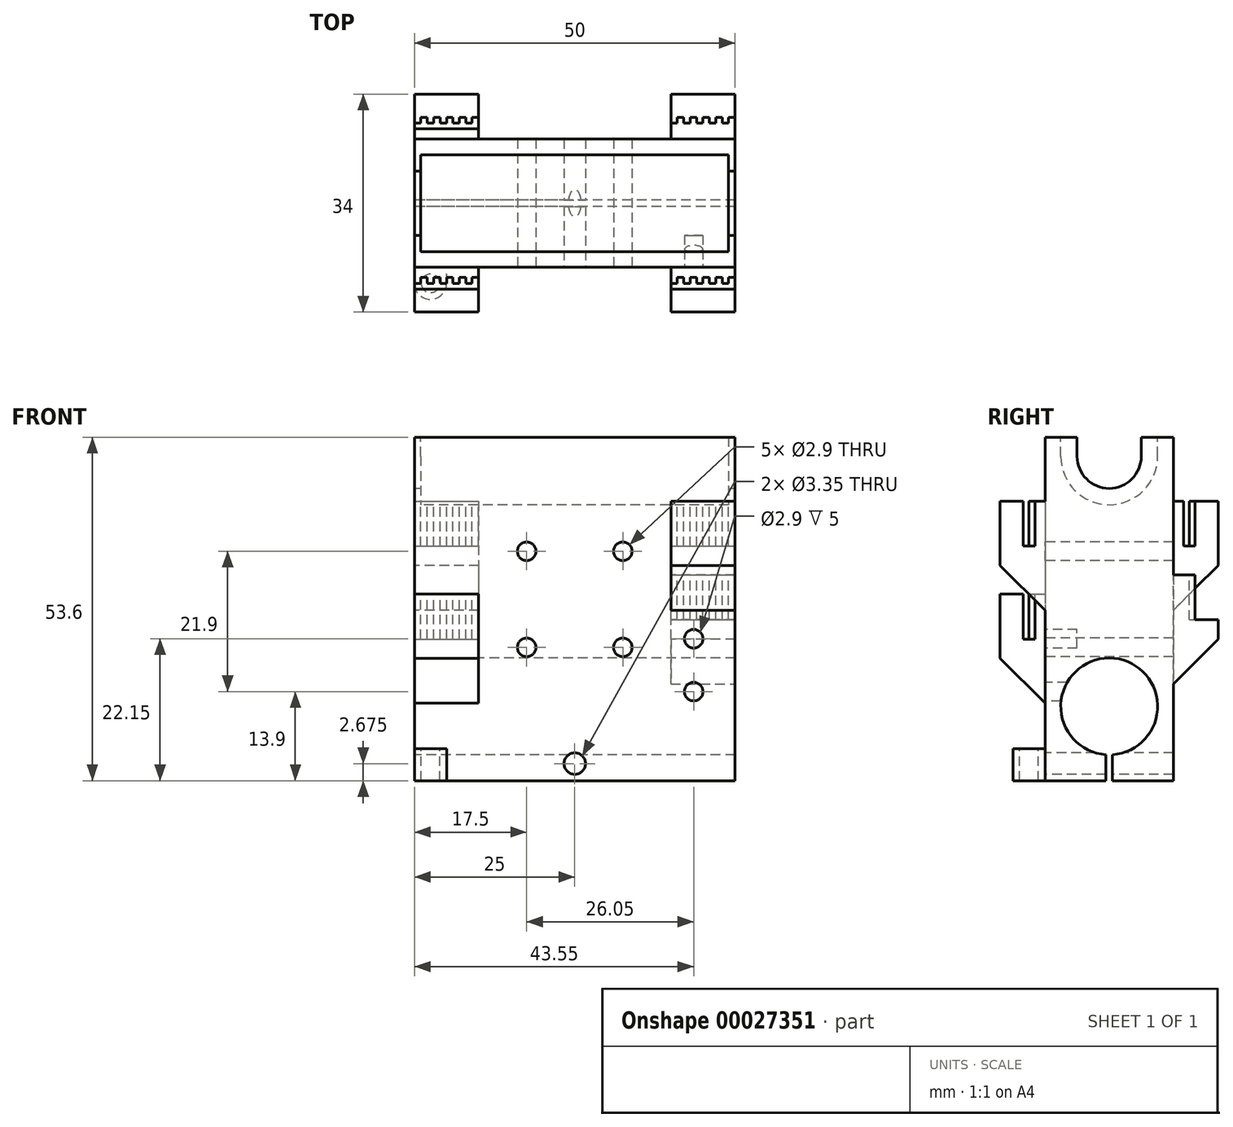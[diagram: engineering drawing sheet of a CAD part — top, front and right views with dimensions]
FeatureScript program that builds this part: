
annotation { "Feature Type Name" : "Feature", "Feature Type Description" : "" }
export const myFeature = defineFeature(function(context is Context, id is Id, definition is map)
    precondition{}
    {
        {
            var Q0;
            Q0=qCreatedBy(makeId("Top.planeOp"),FACE);
            var sketch = newSketch(context, id + "F0", { "sketchPlane" : qUnion([Q0])});
            skLineSegment(sketch, "E0.bottom", {"start": v(0, 0) * mm, "end": v(50, 0) * mm});
            skLineSegment(sketch, "E0.top", {"start": v(0, 20) * mm, "end": v(50, 20) * mm});
            skLineSegment(sketch, "E0.left", {"start": v(0, 0) * mm, "end": v(0, 20) * mm});
            skLineSegment(sketch, "E0.right", {"start": v(50, 0) * mm, "end": v(50, 20) * mm});
            skSolve(sketch);
        }
        {
            var Q0;
            Q0=qSketchRegion(id+"F0",true);
            extrude(context, id + "F1", {"entities" : qUnion([Q0]), "depth" : 50.6 * mm, "hasSecondDirection" : true, "secondDirectionOppositeDirection" : true, "secondDirectionDepth" : 3 * mm});
        }
        {
            var Q0;
            Q0=makeQuery(id+"F1.opExtrude","SWEPT_FACE",FACE,{"disambiguationData":[OSD([sQuery(id+"F0.wireOp",EDGE,"E0.left")])]});
            var sketch = newSketch(context, id + "F2", { "sketchPlane" : qUnion([Q0])});
            skCircle(sketch, "E1", {"center": v(-10, 8.6) * mm, "radius": 7.55 * mm});
            skCircle(sketch, "E2", {"center": v(-10, 47.6) * mm, "radius": 5 * mm});
            skLineSegment(sketch, "E3", {"start": v(-20, 47.6) * mm, "end": v(0, 47.6) * mm, "construction": true});
            skLineSegment(sketch, "E4", {"start": v(-15, 50.6) * mm, "end": v(-15, 47.6) * mm});
            skLineSegment(sketch, "E5", {"start": v(-5, 50.6) * mm, "end": v(-5, 47.6) * mm});
            skLineSegment(sketch, "E6", {"start": v(-20, 8.6) * mm, "end": v(0, 8.6) * mm, "construction": true});
            skLineSegment(sketch, "E7", {"start": v(-10, 8.6) * mm, "end": v(-10, -3) * mm, "construction": true});
            skLineSegment(sketch, "E8", {"start": v(-10, -3) * mm, "end": v(-10.5, -3) * mm});
            skLineSegment(sketch, "E9", {"start": v(-10.5, -3) * mm, "end": v(-10.5, 1.07) * mm});
            skLineSegment(sketch, "E10", {"start": v(-10.5, 1.07) * mm, "end": v(-9.5, 1.07) * mm});
            skLineSegment(sketch, "E11", {"start": v(-9.5, 1.07) * mm, "end": v(-9.5, 0) * mm});
            skLineSegment(sketch, "E12", {"start": v(-9.5, -3) * mm, "end": v(-10, -3) * mm});
            skLineSegment(sketch, "E13", {"start": v(-10, 15.6) * mm, "end": v(-10, 16.15) * mm});
            skLineSegment(sketch, "E14", {"start": v(-10, 15.6) * mm, "end": v(-5.53, 14.68) * mm});
            skLineSegment(sketch, "E15", {"start": v(-10, 15.6) * mm, "end": v(-14.47, 14.68) * mm});
            skCircle(sketch, "E16", {"center": v(-10, 47.6) * mm, "radius": 7.55 * mm});
            skLineSegment(sketch, "E17", {"start": v(-2.45, 47.6) * mm, "end": v(-2.45, 50.6) * mm});
            skLineSegment(sketch, "E18", {"start": v(-17.55, 47.6) * mm, "end": v(-17.55, 50.6) * mm});
            skLineSegment(sketch, "E19", {"start": v(-9.5, -3) * mm, "end": v(-9.5, 0) * mm});
            skSolve(sketch);
        }
        {
            var Q0;
            {var subQ0=sQuery(id+"F2.wireOp",EDGE,"E14");var subQ1=sQuery(id+"F2.wireOp",EDGE,"E1");var subQ3=makeQuery(id+"F2.imprint","INTERSECT",VERTEX,{"disambiguationData":[OD(0.0)],"derivedFrom":[subQ1,subQ0]});Q0=makeQuery(id+"F2.imprint","IMPRINT",FACE,{"disambiguationData":[TD([[makeQuery(id+"F2.imprint","IMPRINT",EDGE,{"disambiguationData":[TD([[subQ3,-1.0]])],"derivedFrom":subQ1}),1.0]])]});}
            var Q1;
            {var subQ0=sQuery(id+"F2.wireOp",EDGE,"E15");var subQ1=sQuery(id+"F2.wireOp",EDGE,"E1");var subQ3=makeQuery(id+"F2.imprint","INTERSECT",VERTEX,{"disambiguationData":[OD(0.0)],"derivedFrom":[subQ1,subQ0]});Q1=makeQuery(id+"F2.imprint","IMPRINT",FACE,{"disambiguationData":[TD([[makeQuery(id+"F2.imprint","IMPRINT",EDGE,{"disambiguationData":[TD([[subQ3,1.0]])],"derivedFrom":subQ1}),1.0]])]});}
            var Q2;
            Q2=makeQuery(id+"F2.imprint","IMPRINT",FACE,{"disambiguationData":[TD([[makeQuery(id+"F2.imprint","IMPRINT",EDGE,{"derivedFrom":sQuery(id+"F2.wireOp",EDGE,"E8")}),-1.0]])]});
            var Q3;
            {var subQ0=sQuery(id+"F2.wireOp",EDGE,"E10");Q3=makeQuery(id+"F2.imprint","IMPRINT",FACE,{"disambiguationData":[TD([[makeQuery(id+"F2.imprint","IMPRINT",EDGE,{"derivedFrom":subQ0}),-1.0]])]});}
            var Q4;
            {var subQ3=sQuery(id+"F2.wireOp",EDGE,"E13");Q4=makeQuery(id+"F2.imprint","IMPRINT",FACE,{"disambiguationData":[TD([[makeQuery(id+"F2.imprint","IMPRINT",EDGE,{"derivedFrom":subQ3}),-1.0]])]});}
            var Q5;
            {var subQ3=sQuery(id+"F2.wireOp",EDGE,"E13");Q5=makeQuery(id+"F2.imprint","IMPRINT",FACE,{"disambiguationData":[TD([[makeQuery(id+"F2.imprint","IMPRINT",EDGE,{"derivedFrom":subQ3}),1.0]])]});}
            var Q6;
            {var subQ7=sQuery(id+"F2.wireOp",EDGE,"E10");Q6=makeQuery(id+"F2.imprint","IMPRINT",FACE,{"disambiguationData":[TD([[makeQuery(id+"F2.imprint","IMPRINT",EDGE,{"derivedFrom":subQ7}),1.0]])]});}
            var Q7;
            {var subQ3=sQuery(id+"F2.wireOp",EDGE,"E5");Q7=makeQuery(id+"F2.imprint","IMPRINT",FACE,{"disambiguationData":[TD([[makeQuery(id+"F2.imprint","IMPRINT",EDGE,{"derivedFrom":subQ3}),-1.0]])]});}
            var Q8;
            {var subQ0=sQuery(id+"F2.wireOp",EDGE,"E4");Q8=makeQuery(id+"F2.imprint","IMPRINT",FACE,{"disambiguationData":[TD([[makeQuery(id+"F2.imprint","IMPRINT",EDGE,{"derivedFrom":subQ0}),1.0]])]});}
            var Q9;
            {var subQ0=sQuery(id+"F2.wireOp",EDGE,"E4");Q9=makeQuery(id+"F2.imprint","IMPRINT",FACE,{"disambiguationData":[TD([[makeQuery(id+"F2.imprint","IMPRINT",EDGE,{"derivedFrom":subQ0}),1.0]])]});}
            var Q10;
            {var subQ3=sQuery(id+"F2.wireOp",EDGE,"E5");Q10=makeQuery(id+"F2.imprint","IMPRINT",FACE,{"disambiguationData":[TD([[makeQuery(id+"F2.imprint","IMPRINT",EDGE,{"derivedFrom":subQ3}),-1.0]])]});}
            var Q11;
            {var subQ1=sQuery(id+"F2.wireOp",EDGE,"E2");var subQ4=makeQuery(id+"F2.imprint","INTERSECT",VERTEX,{"derivedFrom":[subQ1,sQuery(id+"F2.wireOp",EDGE,"E5")]});Q11=makeQuery(id+"F2.imprint","IMPRINT",FACE,{"disambiguationData":[TD([[makeQuery(id+"F2.imprint","IMPRINT",EDGE,{"disambiguationData":[TD([[subQ4,-1.0]])],"derivedFrom":subQ1}),1.0]])]});}
            extrude(context, id + "F3", {"entities" : qUnion([Q0, Q1, Q2, Q3, Q4, Q5, Q6, Q7, Q8, Q9, Q10, Q11]), "operationType" : NewBodyOperationType.REMOVE, "endBound" : BoundingType.THROUGH_ALL, "oppositeDirection" : true, "depth" : 25 * mm});
        }
        {
            var Q0;
            {var subQ3=sQuery(id+"F2.wireOp",EDGE,"E4");Q0=makeQuery(id+"F2.imprint","IMPRINT",FACE,{"disambiguationData":[TD([[makeQuery(id+"F2.imprint","IMPRINT",EDGE,{"derivedFrom":subQ3}),-1.0]])]});}
            var Q1;
            {var subQ3=sQuery(id+"F2.wireOp",EDGE,"E18");Q1=makeQuery(id+"F2.imprint","IMPRINT",FACE,{"disambiguationData":[TD([[makeQuery(id+"F2.imprint","IMPRINT",EDGE,{"derivedFrom":subQ3}),-1.0]])]});}
            var Q2;
            {var subQ3=sQuery(id+"F2.wireOp",EDGE,"E17");Q2=makeQuery(id+"F2.imprint","IMPRINT",FACE,{"disambiguationData":[TD([[makeQuery(id+"F2.imprint","IMPRINT",EDGE,{"derivedFrom":subQ3}),1.0]])]});}
            extrude(context, id + "F4", {"entities" : qUnion([Q0, Q1, Q2]), "operationType" : NewBodyOperationType.REMOVE, "oppositeDirection" : true, "depth" : 49 * mm});
        }
        {
            var Q0;
            {var subQ3=sQuery(id+"F2.wireOp",EDGE,"E4");Q0=makeQuery(id+"F2.imprint","IMPRINT",FACE,{"disambiguationData":[TD([[makeQuery(id+"F2.imprint","IMPRINT",EDGE,{"derivedFrom":subQ3}),-1.0]])]});}
            var Q1;
            {var subQ3=sQuery(id+"F2.wireOp",EDGE,"E18");Q1=makeQuery(id+"F2.imprint","IMPRINT",FACE,{"disambiguationData":[TD([[makeQuery(id+"F2.imprint","IMPRINT",EDGE,{"derivedFrom":subQ3}),-1.0]])]});}
            var Q2;
            {var subQ3=sQuery(id+"F2.wireOp",EDGE,"E17");Q2=makeQuery(id+"F2.imprint","IMPRINT",FACE,{"disambiguationData":[TD([[makeQuery(id+"F2.imprint","IMPRINT",EDGE,{"derivedFrom":subQ3}),1.0]])]});}
            extrude(context, id + "F5", {"entities" : qUnion([Q0, Q1, Q2]), "operationType" : NewBodyOperationType.ADD, "oppositeDirection" : true, "depth" : 16.21 * mm});
        }
        {
            var Q0;
            {var subQ3=sQuery(id+"F2.wireOp",EDGE,"E4");Q0=makeQuery(id+"F2.imprint","IMPRINT",FACE,{"disambiguationData":[TD([[makeQuery(id+"F2.imprint","IMPRINT",EDGE,{"derivedFrom":subQ3}),-1.0]])]});}
            var Q1;
            {var subQ3=sQuery(id+"F2.wireOp",EDGE,"E18");Q1=makeQuery(id+"F2.imprint","IMPRINT",FACE,{"disambiguationData":[TD([[makeQuery(id+"F2.imprint","IMPRINT",EDGE,{"derivedFrom":subQ3}),-1.0]])]});}
            var Q2;
            {var subQ3=sQuery(id+"F2.wireOp",EDGE,"E17");Q2=makeQuery(id+"F2.imprint","IMPRINT",FACE,{"disambiguationData":[TD([[makeQuery(id+"F2.imprint","IMPRINT",EDGE,{"derivedFrom":subQ3}),1.0]])]});}
            extrude(context, id + "F6", {"entities" : qUnion([Q0, Q1, Q2]), "operationType" : NewBodyOperationType.REMOVE, "oppositeDirection" : true, "depth" : 23.25 * mm});
        }
        {
            var Q0;
            {var subQ3=sQuery(id+"F2.wireOp",EDGE,"E4");Q0=makeQuery(id+"F2.imprint","IMPRINT",FACE,{"disambiguationData":[TD([[makeQuery(id+"F2.imprint","IMPRINT",EDGE,{"derivedFrom":subQ3}),-1.0]])]});}
            var Q1;
            {var subQ3=sQuery(id+"F2.wireOp",EDGE,"E18");Q1=makeQuery(id+"F2.imprint","IMPRINT",FACE,{"disambiguationData":[TD([[makeQuery(id+"F2.imprint","IMPRINT",EDGE,{"derivedFrom":subQ3}),-1.0]])]});}
            var Q2;
            {var subQ3=sQuery(id+"F2.wireOp",EDGE,"E17");Q2=makeQuery(id+"F2.imprint","IMPRINT",FACE,{"disambiguationData":[TD([[makeQuery(id+"F2.imprint","IMPRINT",EDGE,{"derivedFrom":subQ3}),1.0]])]});}
            extrude(context, id + "F7", {"entities" : qUnion([Q0, Q1, Q2]), "operationType" : NewBodyOperationType.ADD, "oppositeDirection" : true, "depth" : 1 * mm});
        }
        {
            var Q0;
            Q0=makeQuery(id+"F1.opExtrude","SWEPT_FACE",FACE,{"disambiguationData":[OSD([sQuery(id+"F0.wireOp",EDGE,"E0.bottom")])]});
            var sketch = newSketch(context, id + "F8", { "sketchPlane" : qUnion([Q0])});
            skLineSegment(sketch, "E20.bottom", {"start": v(0, 26.1) * mm, "end": v(10, 26.1) * mm});
            skLineSegment(sketch, "E20.top", {"start": v(0, 6.1) * mm, "end": v(10, 6.1) * mm});
            skLineSegment(sketch, "E20.left", {"start": v(0, 26.1) * mm, "end": v(0, 6.1) * mm});
            skLineSegment(sketch, "E20.right", {"start": v(10, 26.1) * mm, "end": v(10, 6.1) * mm});
            skLineSegment(sketch, "E21.bottom", {"start": v(50, 40.6) * mm, "end": v(40, 40.6) * mm});
            skLineSegment(sketch, "E21.top", {"start": v(50, 20.6) * mm, "end": v(40, 20.6) * mm});
            skLineSegment(sketch, "E21.left", {"start": v(50, 40.6) * mm, "end": v(50, 20.6) * mm});
            skLineSegment(sketch, "E21.right", {"start": v(40, 40.6) * mm, "end": v(40, 20.6) * mm});
            skPoint(sketch, "E22", {"position": v(0, 47.6) * mm});
            skPoint(sketch, "E23", {"position": v(0, 5.6) * mm});
            skSolve(sketch);
        }
        {
            var Q0;
            Q0=qSketchRegion(id+"F8",true);
            extrude(context, id + "F9", {"entities" : qUnion([Q0]), "operationType" : NewBodyOperationType.ADD, "depth" : 7 * mm});
        }
        {
            var Q0;
            Q0=makeQuery(id+"F9.opExtrude","CAP_EDGE",EDGE,{"disambiguationData":[OSD([sQuery(id+"F8.wireOp",EDGE,"E20.top")])],"isStart":false});
            var Q1;
            Q1=makeQuery(id+"F9.opExtrude","CAP_EDGE",EDGE,{"disambiguationData":[OSD([sQuery(id+"F8.wireOp",EDGE,"E21.top")])],"isStart":false});
            chamfer(context, id + "F10", {"entities" : qUnion([Q0, Q1]), "width" : 10 * mm, "tangentPropagation" : true});
        }
        {
            var Q0;
            Q0=makeQuery(id+"F9.opExtrude","SWEPT_FACE",FACE,{"disambiguationData":[OSD([sQuery(id+"F8.wireOp",EDGE,"E20.bottom")])]});
            var sketch = newSketch(context, id + "F11", { "sketchPlane" : qUnion([Q0])});
            skLineSegment(sketch, "E24", {"start": v(-935.9, 0) * mm, "end": v(-935.88, -4.54) * mm});
            skLineSegment(sketch, "E25.left", {"start": v(0, -3.4) * mm, "end": v(0, -1.6) * mm});
            skLineSegment(sketch, "E26", {"start": v(6, -2.5) * mm, "end": v(7, -2.5) * mm});
            skLineSegment(sketch, "E27", {"start": v(4, -2.5) * mm, "end": v(5, -2.5) * mm});
            skLineSegment(sketch, "E28", {"start": v(0, -2.5) * mm, "end": v(1, -2.5) * mm});
            skLineSegment(sketch, "E29", {"start": v(7, -1.6) * mm, "end": v(8, -1.6) * mm});
            skLineSegment(sketch, "E30", {"start": v(2, -2.5) * mm, "end": v(3, -2.5) * mm});
            skLineSegment(sketch, "E31", {"start": v(3, -1.6) * mm, "end": v(4, -1.6) * mm});
            skLineSegment(sketch, "E32", {"start": v(8, -2.5) * mm, "end": v(9, -2.5) * mm});
            skLineSegment(sketch, "E33", {"start": v(8, -1.6) * mm, "end": v(8, -2.5) * mm});
            skLineSegment(sketch, "E34", {"start": v(9, -2.5) * mm, "end": v(9, -1.6) * mm});
            skLineSegment(sketch, "E35", {"start": v(10, -1.6) * mm, "end": v(10, -2.5) * mm});
            skLineSegment(sketch, "E36", {"start": v(6, -1.6) * mm, "end": v(6, -2.5) * mm});
            skLineSegment(sketch, "E37", {"start": v(2, -1.6) * mm, "end": v(2, -2.5) * mm});
            skLineSegment(sketch, "E38", {"start": v(1, -1.6) * mm, "end": v(2, -1.6) * mm});
            skLineSegment(sketch, "E39", {"start": v(1, -2.5) * mm, "end": v(1, -1.6) * mm});
            skLineSegment(sketch, "E40", {"start": v(9, -1.6) * mm, "end": v(10, -1.6) * mm});
            skLineSegment(sketch, "E41", {"start": v(5, -1.6) * mm, "end": v(6, -1.6) * mm});
            skLineSegment(sketch, "E42", {"start": v(5, -2.5) * mm, "end": v(5, -1.6) * mm});
            skLineSegment(sketch, "E43", {"start": v(3, -2.5) * mm, "end": v(3, -1.6) * mm});
            skLineSegment(sketch, "E44", {"start": v(4, -1.6) * mm, "end": v(4, -2.5) * mm});
            skLineSegment(sketch, "E45", {"start": v(7, -2.5) * mm, "end": v(7, -1.6) * mm});
            skLineSegment(sketch, "E46", {"start": v(0, -1.6) * mm, "end": v(0, -2.5) * mm});
            skLineSegment(sketch, "E47", {"start": v(10, -2.5) * mm, "end": v(10, -3.4) * mm});
            skLineSegment(sketch, "E48", {"start": v(0, -3.4) * mm, "end": v(10, -3.4) * mm});
            skLineSegment(sketch, "E49", {"start": v(5.3, -1.6) * mm, "end": v(5.3, 0) * mm});
            skSolve(sketch);
        }
        {
            var Q0;
            Q0=qSketchRegion(id+"F11",true);
            extrude(context, id + "F12", {"entities" : qUnion([Q0]), "operationType" : NewBodyOperationType.REMOVE, "oppositeDirection" : true, "depth" : 7 * mm});
        }
        {
            var Q0;
            Q0=makeQuery(id+"F9.opExtrude","SWEPT_FACE",FACE,{"disambiguationData":[OSD([sQuery(id+"F8.wireOp",EDGE,"E21.bottom")])]});
            var sketch = newSketch(context, id + "F13", { "sketchPlane" : qUnion([Q0])});
            skLineSegment(sketch, "E50.left", {"start": v(40, -3.4) * mm, "end": v(40, -1.6) * mm});
            skLineSegment(sketch, "E51", {"start": v(46, -2.5) * mm, "end": v(47, -2.5) * mm});
            skLineSegment(sketch, "E52", {"start": v(44, -2.5) * mm, "end": v(45, -2.5) * mm});
            skLineSegment(sketch, "E53", {"start": v(40, -2.5) * mm, "end": v(41, -2.5) * mm});
            skLineSegment(sketch, "E54", {"start": v(47, -1.6) * mm, "end": v(48, -1.6) * mm});
            skLineSegment(sketch, "E55", {"start": v(42, -2.5) * mm, "end": v(43, -2.5) * mm});
            skLineSegment(sketch, "E56", {"start": v(43, -1.6) * mm, "end": v(44, -1.6) * mm});
            skLineSegment(sketch, "E57", {"start": v(48, -2.5) * mm, "end": v(49, -2.5) * mm});
            skLineSegment(sketch, "E58", {"start": v(48, -1.6) * mm, "end": v(48, -2.5) * mm});
            skLineSegment(sketch, "E59", {"start": v(49, -2.5) * mm, "end": v(49, -1.6) * mm});
            skLineSegment(sketch, "E60", {"start": v(50, -1.6) * mm, "end": v(50, -2.5) * mm});
            skLineSegment(sketch, "E61", {"start": v(46, -1.6) * mm, "end": v(46, -2.5) * mm});
            skLineSegment(sketch, "E62", {"start": v(42, -1.6) * mm, "end": v(42, -2.5) * mm});
            skLineSegment(sketch, "E63", {"start": v(41, -1.6) * mm, "end": v(42, -1.6) * mm});
            skLineSegment(sketch, "E64", {"start": v(41, -2.5) * mm, "end": v(41, -1.6) * mm});
            skLineSegment(sketch, "E65", {"start": v(49, -1.6) * mm, "end": v(50, -1.6) * mm});
            skLineSegment(sketch, "E66", {"start": v(45, -1.6) * mm, "end": v(46, -1.6) * mm});
            skLineSegment(sketch, "E67", {"start": v(45, -2.5) * mm, "end": v(45, -1.6) * mm});
            skLineSegment(sketch, "E68", {"start": v(43, -2.5) * mm, "end": v(43, -1.6) * mm});
            skLineSegment(sketch, "E69", {"start": v(44, -1.6) * mm, "end": v(44, -2.5) * mm});
            skLineSegment(sketch, "E70", {"start": v(47, -2.5) * mm, "end": v(47, -1.6) * mm});
            skLineSegment(sketch, "E71", {"start": v(40, -1.6) * mm, "end": v(40, -2.5) * mm});
            skLineSegment(sketch, "E72", {"start": v(50, -2.5) * mm, "end": v(50, -3.4) * mm});
            skLineSegment(sketch, "E73", {"start": v(40, -3.4) * mm, "end": v(50, -3.4) * mm});
            skLineSegment(sketch, "E74", {"start": v(45.23, -1.6) * mm, "end": v(45.23, 0) * mm});
            skSolve(sketch);
        }
        {
            var Q0;
            Q0=qSketchRegion(id+"F13",true);
            extrude(context, id + "F14", {"entities" : qUnion([Q0]), "operationType" : NewBodyOperationType.REMOVE, "oppositeDirection" : true, "depth" : 7 * mm});
        }
        {
            var Q0;
            Q0=makeQuery(id+"F1.opExtrude","SWEPT_FACE",FACE,{"disambiguationData":[OSD([sQuery(id+"F0.wireOp",EDGE,"E0.top")])]});
            var sketch = newSketch(context, id + "F15", { "sketchPlane" : qUnion([Q0])});
            skLineSegment(sketch, "E75.bottom", {"start": v(-50, 9.1) * mm, "end": v(-40, 9.1) * mm});
            skLineSegment(sketch, "E75.top", {"start": v(-50, 29.1) * mm, "end": v(-40, 29.1) * mm});
            skLineSegment(sketch, "E75.left", {"start": v(-50, 9.1) * mm, "end": v(-50, 29.1) * mm});
            skLineSegment(sketch, "E75.right", {"start": v(-40, 9.1) * mm, "end": v(-40, 29.1) * mm});
            skLineSegment(sketch, "E76.bottom", {"start": v(0, 40.6) * mm, "end": v(-10, 40.6) * mm});
            skLineSegment(sketch, "E76.top", {"start": v(0, 20.6) * mm, "end": v(-10, 20.6) * mm});
            skLineSegment(sketch, "E76.left", {"start": v(0, 40.6) * mm, "end": v(0, 20.6) * mm});
            skLineSegment(sketch, "E76.right", {"start": v(-10, 40.6) * mm, "end": v(-10, 20.6) * mm});
            skSolve(sketch);
        }
        {
            var Q0;
            Q0=qSketchRegion(id+"F15",true);
            extrude(context, id + "F16", {"entities" : qUnion([Q0]), "operationType" : NewBodyOperationType.ADD, "depth" : 7 * mm});
        }
        {
            var Q0;
            Q0=makeQuery(id+"F16.opExtrude","SWEPT_FACE",FACE,{"disambiguationData":[OSD([sQuery(id+"F15.wireOp",EDGE,"E75.top")])]});
            var sketch = newSketch(context, id + "F17", { "sketchPlane" : qUnion([Q0])});
            skLineSegment(sketch, "E77.left", {"start": v(40, 21.6) * mm, "end": v(40, 23.4) * mm});
            skLineSegment(sketch, "E78", {"start": v(46, 22.5) * mm, "end": v(47, 22.5) * mm});
            skLineSegment(sketch, "E79", {"start": v(44, 22.5) * mm, "end": v(45, 22.5) * mm});
            skLineSegment(sketch, "E80", {"start": v(40, 22.5) * mm, "end": v(41, 22.5) * mm});
            skLineSegment(sketch, "E81", {"start": v(47, 23.4) * mm, "end": v(48, 23.4) * mm});
            skLineSegment(sketch, "E82", {"start": v(42, 22.5) * mm, "end": v(43, 22.5) * mm});
            skLineSegment(sketch, "E83", {"start": v(43, 23.4) * mm, "end": v(44, 23.4) * mm});
            skLineSegment(sketch, "E84", {"start": v(48, 22.5) * mm, "end": v(49, 22.5) * mm});
            skLineSegment(sketch, "E85", {"start": v(48, 23.4) * mm, "end": v(48, 22.5) * mm});
            skLineSegment(sketch, "E86", {"start": v(49, 22.5) * mm, "end": v(49, 23.4) * mm});
            skLineSegment(sketch, "E87", {"start": v(50, 23.4) * mm, "end": v(50, 22.5) * mm});
            skLineSegment(sketch, "E88", {"start": v(46, 23.4) * mm, "end": v(46, 22.5) * mm});
            skLineSegment(sketch, "E89", {"start": v(42, 23.4) * mm, "end": v(42, 22.5) * mm});
            skLineSegment(sketch, "E90", {"start": v(41, 23.4) * mm, "end": v(42, 23.4) * mm});
            skLineSegment(sketch, "E91", {"start": v(41, 22.5) * mm, "end": v(41, 23.4) * mm});
            skLineSegment(sketch, "E92", {"start": v(49, 23.4) * mm, "end": v(50, 23.4) * mm});
            skLineSegment(sketch, "E93", {"start": v(45, 23.4) * mm, "end": v(46, 23.4) * mm});
            skLineSegment(sketch, "E94", {"start": v(45, 22.5) * mm, "end": v(45, 23.4) * mm});
            skLineSegment(sketch, "E95", {"start": v(43, 22.5) * mm, "end": v(43, 23.4) * mm});
            skLineSegment(sketch, "E96", {"start": v(44, 23.4) * mm, "end": v(44, 22.5) * mm});
            skLineSegment(sketch, "E97", {"start": v(47, 22.5) * mm, "end": v(47, 23.4) * mm});
            skLineSegment(sketch, "E98", {"start": v(40, 23.4) * mm, "end": v(40, 22.5) * mm});
            skLineSegment(sketch, "E99", {"start": v(50, 22.5) * mm, "end": v(50, 21.6) * mm});
            skLineSegment(sketch, "E100", {"start": v(40, 21.6) * mm, "end": v(50, 21.6) * mm});
            skLineSegment(sketch, "E101", {"start": v(45, 21.6) * mm, "end": v(45, 20) * mm});
            skSolve(sketch);
        }
        {
            var Q0;
            {var subQ4=sQuery(id+"F17.wireOp",EDGE,"E77.left");Q0=makeQuery(id+"F17.imprint","IMPRINT",FACE,{"disambiguationData":[TD([[makeQuery(id+"F17.imprint","IMPRINT",EDGE,{"derivedFrom":subQ4}),1.0]])]});}
            extrude(context, id + "F18", {"entities" : qUnion([Q0]), "operationType" : NewBodyOperationType.REMOVE, "oppositeDirection" : true, "depth" : 7 * mm});
        }
        {
            var Q0;
            Q0=makeQuery(id+"F16.opExtrude","SWEPT_FACE",FACE,{"disambiguationData":[OSD([sQuery(id+"F15.wireOp",EDGE,"E76.bottom")])]});
            var sketch = newSketch(context, id + "F19", { "sketchPlane" : qUnion([Q0])});
            skLineSegment(sketch, "E102", {"start": v(6, 22.5) * mm, "end": v(7, 22.5) * mm});
            skLineSegment(sketch, "E103", {"start": v(4, 22.5) * mm, "end": v(5, 22.5) * mm});
            skLineSegment(sketch, "E104", {"start": v(0, 22.5) * mm, "end": v(1, 22.5) * mm});
            skLineSegment(sketch, "E105", {"start": v(7, 23.4) * mm, "end": v(8, 23.4) * mm});
            skLineSegment(sketch, "E106", {"start": v(2, 22.5) * mm, "end": v(3, 22.5) * mm});
            skLineSegment(sketch, "E107", {"start": v(3, 23.4) * mm, "end": v(4, 23.4) * mm});
            skLineSegment(sketch, "E108", {"start": v(8, 22.5) * mm, "end": v(9, 22.5) * mm});
            skLineSegment(sketch, "E109", {"start": v(8, 23.4) * mm, "end": v(8, 22.5) * mm});
            skLineSegment(sketch, "E110", {"start": v(9, 22.5) * mm, "end": v(9, 23.4) * mm});
            skLineSegment(sketch, "E111", {"start": v(10, 23.4) * mm, "end": v(10, 22.5) * mm});
            skLineSegment(sketch, "E112", {"start": v(6, 23.4) * mm, "end": v(6, 22.5) * mm});
            skLineSegment(sketch, "E113", {"start": v(2, 23.4) * mm, "end": v(2, 22.5) * mm});
            skLineSegment(sketch, "E114", {"start": v(1, 23.4) * mm, "end": v(2, 23.4) * mm});
            skLineSegment(sketch, "E115", {"start": v(1, 22.5) * mm, "end": v(1, 23.4) * mm});
            skLineSegment(sketch, "E116", {"start": v(9, 23.4) * mm, "end": v(10, 23.4) * mm});
            skLineSegment(sketch, "E117", {"start": v(5, 23.4) * mm, "end": v(6, 23.4) * mm});
            skLineSegment(sketch, "E118", {"start": v(5, 22.5) * mm, "end": v(5, 23.4) * mm});
            skLineSegment(sketch, "E119", {"start": v(3, 22.5) * mm, "end": v(3, 23.4) * mm});
            skLineSegment(sketch, "E120", {"start": v(4, 23.4) * mm, "end": v(4, 22.5) * mm});
            skLineSegment(sketch, "E121", {"start": v(7, 22.5) * mm, "end": v(7, 23.4) * mm});
            skLineSegment(sketch, "E122", {"start": v(10, 22.5) * mm, "end": v(10, 21.6) * mm});
            skLineSegment(sketch, "E123", {"start": v(0, 21.6) * mm, "end": v(10, 21.6) * mm});
            skLineSegment(sketch, "E124", {"start": v(5, 21.6) * mm, "end": v(5, 20) * mm});
            skLineSegment(sketch, "E125", {"start": v(0, 21.6) * mm, "end": v(0, 22.5) * mm});
            skSolve(sketch);
        }
        {
            var Q0;
            Q0=makeQuery(id+"F19.imprint","IMPRINT",FACE,{"disambiguationData":[TD([[makeQuery(id+"F19.imprint","IMPRINT",EDGE,{"derivedFrom":sQuery(id+"F19.wireOp",EDGE,"E102")}),-1.0]])]});
            extrude(context, id + "F20", {"entities" : qUnion([Q0]), "operationType" : NewBodyOperationType.REMOVE, "oppositeDirection" : true, "depth" : 7 * mm});
        }
        {
            var Q0;
            Q0=makeQuery(id+"F16.opExtrude","CAP_EDGE",EDGE,{"disambiguationData":[OSD([sQuery(id+"F15.wireOp",EDGE,"E76.top")])],"isStart":false});
            var Q1;
            Q1=makeQuery(id+"F16.opExtrude","CAP_EDGE",EDGE,{"disambiguationData":[OSD([sQuery(id+"F15.wireOp",EDGE,"E75.bottom")])],"isStart":false});
            chamfer(context, id + "F21", {"entities" : qUnion([Q0, Q1]), "width" : 10 * mm, "tangentPropagation" : true});
        }
        {
            var Q0;
            Q0=makeQuery(id+"F1.opExtrude","SWEPT_FACE",FACE,{"disambiguationData":[OSD([sQuery(id+"F0.wireOp",EDGE,"E0.bottom")])]});
            var sketch = newSketch(context, id + "F22", { "sketchPlane" : qUnion([Q0])});
            skCircle(sketch, "E126", {"center": v(17.5, 32.8) * mm, "radius": 1.45 * mm});
            skCircle(sketch, "E127", {"center": v(32.5, 32.8) * mm, "radius": 1.45 * mm});
            skCircle(sketch, "E128", {"center": v(17.5, 17.8) * mm, "radius": 1.45 * mm});
            skCircle(sketch, "E129", {"center": v(32.5, 17.8) * mm, "radius": 1.45 * mm});
            skLineSegment(sketch, "E130", {"start": v(17.5, 32.8) * mm, "end": v(0, 32.8) * mm});
            skLineSegment(sketch, "E131", {"start": v(32.5, 17.8) * mm, "end": v(50, 17.8) * mm});
            skLineSegment(sketch, "E132", {"start": v(32.5, 32.8) * mm, "end": v(32.5, 50.6) * mm});
            skLineSegment(sketch, "E133", {"start": v(17.5, 17.8) * mm, "end": v(17.5, 0) * mm});
            skCircle(sketch, "E134", {"center": v(25, -0.32) * mm, "radius": 1.68 * mm});
            skLineSegment(sketch, "E135", {"start": v(25, -3) * mm, "end": v(25, 13.82) * mm, "construction": true});
            skSolve(sketch);
        }
        {
            var Q0;
            Q0=qSketchRegion(id+"F22",true);
            var Q1;
            Q1=makeQuery(id+"F22.imprint","IMPRINT",FACE,{"disambiguationData":[TD([[makeQuery(id+"F22.imprint","IMPRINT",EDGE,{"derivedFrom":sQuery(id+"F22.wireOp",EDGE,"E126")}),1.0]])]});
            var Q2;
            Q2=makeQuery(id+"F22.imprint","IMPRINT",FACE,{"disambiguationData":[TD([[makeQuery(id+"F22.imprint","IMPRINT",EDGE,{"derivedFrom":sQuery(id+"F22.wireOp",EDGE,"E127")}),1.0]])]});
            var Q3;
            Q3=makeQuery(id+"F22.imprint","IMPRINT",FACE,{"disambiguationData":[TD([[makeQuery(id+"F22.imprint","IMPRINT",EDGE,{"derivedFrom":sQuery(id+"F22.wireOp",EDGE,"E129")}),1.0]])]});
            var Q4;
            Q4=makeQuery(id+"F22.imprint","IMPRINT",FACE,{"disambiguationData":[TD([[makeQuery(id+"F22.imprint","IMPRINT",EDGE,{"derivedFrom":sQuery(id+"F22.wireOp",EDGE,"E128")}),1.0]])]});
            extrude(context, id + "F23", {"entities" : qUnion([Q0, Q1, Q2, Q3, Q4]), "operationType" : NewBodyOperationType.REMOVE, "endBound" : BoundingType.THROUGH_ALL, "oppositeDirection" : true, "depth" : 25 * mm});
        }
        {
            var Q0;
            Q0=makeQuery(id+"F1.opExtrude","SWEPT_FACE",FACE,{"disambiguationData":[OSD([sQuery(id+"F0.wireOp",EDGE,"E0.bottom")])]});
            var sketch = newSketch(context, id + "F24", { "sketchPlane" : qUnion([Q0])});
            skCircle(sketch, "E136", {"center": v(43.55, 19.15) * mm, "radius": 1.45 * mm});
            skCircle(sketch, "E137", {"center": v(43.55, 10.9) * mm, "radius": 1.45 * mm});
            skSolve(sketch);
        }
        {
            var Q0;
            Q0=qSketchRegion(id+"F24",true);
            extrude(context, id + "F25", {"entities" : qUnion([Q0]), "operationType" : NewBodyOperationType.REMOVE, "oppositeDirection" : true, "depth" : 5 * mm});
        }
        {
            var Q0;
            Q0=makeQuery(id+"F1.opExtrude","SWEPT_FACE",FACE,{"disambiguationData":[OSD([sQuery(id+"F0.wireOp",EDGE,"E0.bottom")])]});
            var sketch = newSketch(context, id + "F26", { "sketchPlane" : qUnion([Q0])});
            skLineSegment(sketch, "E138.bottom", {"start": v(0, -3) * mm, "end": v(5, -3) * mm});
            skLineSegment(sketch, "E138.top", {"start": v(0, 2) * mm, "end": v(5, 2) * mm});
            skLineSegment(sketch, "E138.left", {"start": v(0, -3) * mm, "end": v(0, 2) * mm});
            skLineSegment(sketch, "E138.right", {"start": v(5, -3) * mm, "end": v(5, 2) * mm});
            skSolve(sketch);
        }
        {
            var Q0;
            Q0=qSketchRegion(id+"F26",true);
            extrude(context, id + "F27", {"entities" : qUnion([Q0]), "operationType" : NewBodyOperationType.ADD, "depth" : 5 * mm});
        }
        {
            var Q0;
            Q0=makeQuery(id+"F27.opExtrude","SWEPT_FACE",FACE,{"disambiguationData":[OSD([sQuery(id+"F26.wireOp",EDGE,"E138.top")])]});
            var sketch = newSketch(context, id + "F28", { "sketchPlane" : qUnion([Q0])});
            skCircle(sketch, "E139", {"center": v(2.5, -2.5) * mm, "radius": 1.45 * mm});
            skLineSegment(sketch, "E140", {"start": v(0, -2.5) * mm, "end": v(5, -2.5) * mm});
            skSolve(sketch);
        }
        {
            var Q0;
            Q0=qSketchRegion(id+"F28",true);
            extrude(context, id + "F29", {"entities" : qUnion([Q0]), "operationType" : NewBodyOperationType.REMOVE, "oppositeDirection" : true, "depth" : 25 * mm});
        }
        {
            var Q0;
            Q0=makeQuery(id+"F27.opExtrude","CAP_EDGE",EDGE,{"disambiguationData":[OSD([sQuery(id+"F26.wireOp",EDGE,"E138.left")])],"isStart":false});
            var Q1;
            Q1=makeQuery(id+"F27.opExtrude","CAP_EDGE",EDGE,{"disambiguationData":[OSD([sQuery(id+"F26.wireOp",EDGE,"E138.right")])],"isStart":false});
            fillet(context, id + "F30", {"entities" : qUnion([Q0, Q1]), "radius" : 2.5 * mm, "tangentPropagation" : true, "allowEdgeOverflow" : false});
        }
    });
